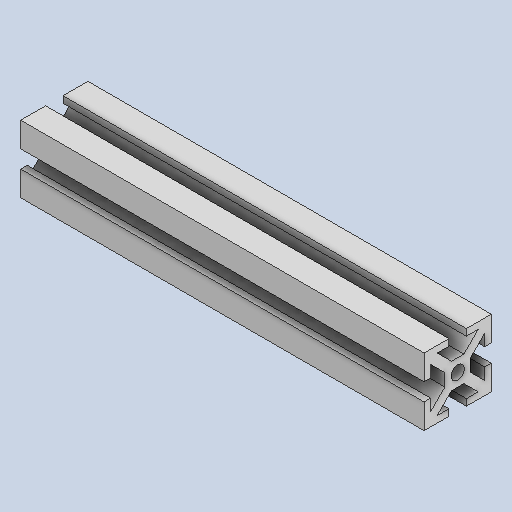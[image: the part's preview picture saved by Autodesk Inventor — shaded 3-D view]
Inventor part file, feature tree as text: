
AUTODESK INVENTOR PART (.ipt)
format: ipt  version: 2023 (Build 270158030, 158C)  size: 160,256 bytes
history: native  units: in
note: dims shown in document units (in); Inventor stores cm internally (conversion verified against a paired STEP export)
features: extrude x1, sketch x1
ambient origin geometry x8: Origin, YZ Plane, XZ Plane, XY Plane, X Axis, Y Axis, Z Axis, Center Point
bodies: Solid1 (feature_tree)
feature tree (2):
  extrude  "Extrusion1"  Depth=0.0975in
  sketch  "Sketch1"  dims[d2=0.37in d3=0.0975in d7=0.0975in d10=0.0975in d11=1.0in d13=0.0975in d16=0.0975in d17=0.37in d18=1.0in d23=0.0975in d24=1.0in d25=1.0in d32=0.175in d33=0.175in d35=135.0deg d36=0.175in d37=0.175in d38=0.0975in d40=0.175in d41=0.175in d42=0.175in d43=0.175in d44=0.2in d45=6.0in d46=0.0in]
